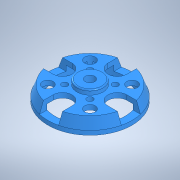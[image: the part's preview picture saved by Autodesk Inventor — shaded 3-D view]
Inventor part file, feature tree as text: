
AUTODESK INVENTOR PART (.ipt)
format: ipt  version: 2022 (Build 260153000, 153)  size: 239,616 bytes
history: native  units: in
note: dims shown in document units (in); Inventor stores cm internally (conversion verified against a paired STEP export)
features: sketch x3, extrude x2, revolve x1, chamfer x1, fillet x1
ambient origin geometry x8: Origin, YZ Plane, XZ Plane, XY Plane, X Axis, Y Axis, Z Axis, Center Point
bodies: Solid1 (feature_tree)
feature tree (8):
  revolve  "Revolution1"  [1 undecoded]
  extrude  "Extrusion1"  Depth=0.0787in
  extrude  "Extrusion2"  Depth=0.0689in
  chamfer  "Chamfer1"  Distance=0.0787in
  fillet  "Fillet1"  [1 undecoded]
  sketch  "Sketch1"  dims[d0=0.6929in d1=0.2362in]
  sketch  "Sketch2"  dims[d2=0.2165in d3=0.0787in]
  sketch  "Sketch3"  dims[d4=0.6299in d5=0.0689in d6=0.0787in d7=90.0deg d8=0.315in d9=0.9055in d10=0.375in d11=0.5906in d12=0.9843in d13=45.0deg d14=0.0984in d15=0.1772in d16=1.5748in d18=360.0deg d20=0.1673in d21=0.0in d22=0.1181in d23=0.315in d24=0.1575in d25=0.0in d26=0.1575in d27=0.125in d28=0.1374in d29=0.0197in]
note: 2 required parameter values undecoded (feature->parameter linkage not recoverable at this tier; creation-order binding heuristic only, values carry confidence <= 0.55)